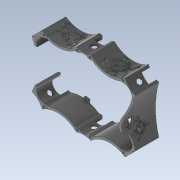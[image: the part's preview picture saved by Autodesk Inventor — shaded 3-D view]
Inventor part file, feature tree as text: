
AUTODESK INVENTOR PART (.ipt)
format: ipt  version: 2020 (Build 240168000, 168)  size: 5,370,368 bytes
history: native  units: mm
features: projected_geometry x82, extrude x36, sketch x35, other x23, reference x22, chamfer x10, plane x10, hole x3, fillet x3, emboss x3, mirror x3
ambient origin geometry x8: Origin, YZ Plane, XZ Plane, XY Plane, X Axis, Y Axis, Z Axis, Center Point
bodies: Solid1 (feature_tree), Solid2 (feature_tree)
feature tree (230):
  other  "BodyTop2.ipt"
  extrude  "Extrusion1"  Depth=4.404mm
  extrude  "Extrusion2"  Depth=22.0mm
  extrude  "Extrusion3"  Depth=35.3mm
  hole  "Hole2"  [1 undecoded]
  extrude  "Extrusion17"  Depth=19.0mm
  sketch  "Sketch27"  dims[d10=6.0mm d11=10.0mm]
  hole  "Hole4"  [1 undecoded]
  extrude  "Extrusion27"  Depth=100.0mm
  extrude  "Extrusion29"  Depth=17.453293mm
  extrude  "Extrusion30"  Depth=13.962634mm
  extrude  "Extrusion31"  Depth=4.8mm
  extrude  "Extrusion34"  Depth=6.2mm
  hole  "Hole6"  [1 undecoded]
  chamfer  "Chamfer12"  Distance=155.440339mm
  extrude  "Extrusion46"  Depth=2.0mm
  chamfer  "Chamfer13"  Distance=2.0mm
  chamfer  "Chamfer14"  Distance=4.8mm
  chamfer  "Chamfer15"  Distance=33.0mm
  chamfer  "Chamfer16"  Distance=2.5mm
  chamfer  "Chamfer17"  Distance=2.0mm
  chamfer  "Chamfer18"  Distance=2.5mm
  sketch  "Sketch55"  dims[d20=6.2mm d21=6.2mm]
  plane  "Work Plane2"
  extrude  "Extrusion55"  Depth=2.0mm
  extrude  "Extrusion56"  Depth=14.0mm
  extrude  "Extrusion57"  Depth=2.0mm
  extrude  "Extrusion61"  Depth=106.731156mm
  extrude  "Extrusion62"  Depth=94.331156mm
  extrude  "Extrusion63"  Depth=10.0mm TaperAngle=0.0deg
  extrude  "Extrusion64"  Depth=146.583126mm
  extrude  "Extrusion69"  Depth=113.583126mm
  extrude  "Extrusion70"  Depth=207.691804mm
  chamfer  "Chamfer19"  Distance=235.691804mm
  extrude  "Extrusion71"  Depth=89.108678mm
  extrude  "Extrusion72"  Depth=12.4mm
  extrude  "Extrusion73"  Depth=56.108678mm
  extrude  "Extrusion74"  Depth=12.4mm
  chamfer  "Chamfer20"  Distance=23.0mm
  extrude  "Extrusion78"  Depth=142.600153mm
  extrude  "Extrusion79"  Depth=170.600153mm
  sketch  "Sketch82"  dims[d37=6.2mm]
  extrude  "Extrusion81"  Depth=142.600153mm
  extrude  "Extrusion82"  Depth=19.0mm TaperAngle=0.0deg
  extrude  "Extrusion83"  Depth=5.0mm TaperAngle=0.0deg
  extrude  "Extrusion84"  Depth=9.0mm TaperAngle=0.0deg
  plane  "Work Plane5"
  extrude  "Extrusion86"  Depth=3.2505mm
  fillet  "Fillet2"  Radius=3.2505mm
  extrude  "Extrusion87"  Depth=3.2505mm
  fillet  "Fillet4"  Radius=3.2505mm
  plane  "Work Plane6"
  extrude  "Extrusion89"  Depth=3.2505mm
  fillet  "Fillet5"  Radius=2.4mm
  extrude  "Extrusion90"  Depth=3.1mm
  plane  "Work Plane7"
  emboss  "Emboss1"
  plane  "Work Plane8"
  extrude  "Extrusion92"  Depth=6.0mm
  plane  "Work Plane10"
  extrude  "Extrusion93"  Depth=4.5mm
  plane  "Work Plane11"
  plane  "Work Plane13"
  plane  "Work Plane14"
  plane  "Work Plane15"
  extrude  "Extrusion94"  Depth=4.5mm
  mirror  "Mirror3"
  mirror  "Mirror4"
  emboss  "Emboss3"
  emboss  "Emboss4"
  mirror  "Mirror5"
  chamfer  "Chamfer21"  Distance=1.7mm
  sketch  "Sketch1"  dims[d0=50.0mm d1=4.404mm]
  reference  "Reference1"
  reference  "Reference2"
  reference  "Reference3"
  reference  "Reference4"
  sketch  "Sketch2"  dims[d2=135.0deg d3=22.0mm]
  reference  "Reference5"
  reference  "Reference6"
  reference  "Reference7"
  reference  "Reference8"
  reference  "Reference9"
  reference  "Reference10"
  reference  "Reference11"
  reference  "Reference12"
  reference  "Reference13"
  reference  "Reference14"
  reference  "Reference15"
  reference  "Reference16"
  sketch  "Sketch3"  dims[d4=35.3mm d5=35.3mm]
  projected_geometry  "Projected Loop1"
  projected_geometry  "Projected Loop2"
  sketch  "Sketch6"  dims[d6=98.287843mm d7=10.0mm]
  reference  "Reference23"
  reference  "Reference24"
  reference  "Reference25"
  reference  "Reference26"
  reference  "Reference27"
  reference  "Reference28"
  sketch  "Sketch18"  dims[d8=19.0mm d9=19.0mm]
  projected_geometry  "Projected Loop13"
  projected_geometry  "Projected Loop19"
  projected_geometry  "Projected Loop23"
  projected_geometry  "Projected Loop28"
  projected_geometry  "Projected Loop29"
  projected_geometry  "Projected Loop30"
  sketch  "Sketch28"  dims[d12=19.0mm d13=100.0mm]
  projected_geometry  "Projected Loop31"
  projected_geometry  "Projected Loop33"
  projected_geometry  "Projected Loop34"
  sketch  "Sketch32"  dims[d14=30.0mm d15=17.453293mm]
  projected_geometry  "Projected Loop35"
  projected_geometry  "Projected Loop36"
  projected_geometry  "Projected Loop37"
  projected_geometry  "Projected Loop38"
  projected_geometry  "Projected Loop39"
  projected_geometry  "Projected Loop40"
  projected_geometry  "Projected Loop41"
  projected_geometry  "Projected Loop42"
  projected_geometry  "Projected Loop43"
  projected_geometry  "Projected Loop44"
  projected_geometry  "Projected Loop45"
  projected_geometry  "Projected Loop46"
  sketch  "Sketch35"  dims[d16=30.0mm d17=13.962634mm]
  projected_geometry  "Projected Loop52"
  sketch  "Sketch46"  dims[d18=2.0mm d19=4.8mm]
  projected_geometry  "Projected Loop74"
  sketch  "Sketch56"  dims[d22=33.0mm d23=2.5mm]
  projected_geometry  "Projected Loop75"
  sketch  "Sketch57"  dims[d24=2.0mm]
  projected_geometry  "Projected Loop76"
  sketch  "Sketch60"  dims[d25=2.5mm]
  sketch  "Sketch61"  dims[d26=2.0mm]
  projected_geometry  "Projected Loop77"
  other  "Solid1::BodyTop2.ipt"
  other  "TaggingFeature1"
  sketch  "Sketch62"  dims[d27=2.0mm]
  projected_geometry  "Projected Loop78"
  projected_geometry  "Projected Loop79"
  sketch  "Sketch69"  dims[d28=90.0deg]
  projected_geometry  "Projected Loop84"
  sketch  "Sketch70"  dims[d29=6.2mm]
  projected_geometry  "Projected Loop85"
  sketch  "Sketch71"  dims[d30=6.2mm]
  projected_geometry  "Projected Loop86"
  projected_geometry  "Projected Loop87"
  projected_geometry  "Projected Loop88"
  projected_geometry  "Projected Loop89"
  projected_geometry  "Projected Loop90"
  projected_geometry  "Projected Loop91"
  projected_geometry  "Projected Loop92"
  sketch  "Sketch72"  dims[d31=33.0mm]
  projected_geometry  "Projected Loop93"
  sketch  "Sketch73"  dims[d32=2.0mm]
  projected_geometry  "Projected Loop94"
  sketch  "Sketch74"  dims[d33=2.5mm]
  projected_geometry  "Projected Loop95"
  sketch  "Sketch78"  dims[d35=2.0mm]
  projected_geometry  "Projected Loop105"
  projected_geometry  "Projected Loop107"
  sketch  "Sketch79"  dims[d36=4.8mm]
  projected_geometry  "Projected Loop108"
  projected_geometry  "Projected Loop111"
  projected_geometry  "Projected Loop112"
  projected_geometry  "Projected Loop113"
  projected_geometry  "Projected Loop114"
  projected_geometry  "Projected Loop115"
  sketch  "Sketch83"  dims[d38=6.2mm]
  projected_geometry  "Projected Loop116"
  projected_geometry  "Projected Loop117"
  projected_geometry  "Projected Loop118"
  projected_geometry  "Projected Loop119"
  sketch  "Sketch84"  dims[d39=33.0mm]
  projected_geometry  "Projected Loop120"
  projected_geometry  "Projected Loop121"
  projected_geometry  "Projected Loop122"
  projected_geometry  "Projected Loop123"
  projected_geometry  "Projected Loop125"
  projected_geometry  "Projected Loop126"
  sketch  "Sketch89"  dims[d40=2.5mm]
  sketch  "Sketch91"  dims[d41=2.0mm]
  projected_geometry  "Projected Loop128"
  projected_geometry  "Projected Loop129"
  projected_geometry  "Projected Loop130"
  projected_geometry  "Projected Loop131"
  projected_geometry  "Projected Loop132"
  projected_geometry  "Projected Loop133"
  projected_geometry  "Projected Loop134"
  projected_geometry  "Projected Loop135"
  projected_geometry  "Projected Loop136"
  sketch  "Sketch93"  dims[d42=2.5mm]
  projected_geometry  "Projected Loop138"
  sketch  "Sketch94"  dims[d43=2.0mm]
  projected_geometry  "Projected Loop139"
  projected_geometry  "Projected Loop140"
  projected_geometry  "Projected Loop141"
  projected_geometry  "Projected Loop142"
  projected_geometry  "Projected Loop143"
  projected_geometry  "Projected Loop144"
  sketch  "Sketch96"  dims[d44=2.0mm]
  projected_geometry  "Projected Loop147"
  sketch  "Sketch97"  dims[d45=2.5mm]
  projected_geometry  "Projected Loop148"
  sketch  "Sketch98"  dims[d46=19.402mm]
  projected_geometry  "Projected Loop149"
  projected_geometry  "Projected Loop150"
  projected_geometry  "Projected Loop151"
  sketch  "Sketch99"  dims[d47=169.440339mm d48=155.440339mm d58=2.0mm d59=2.0mm d71=4.8mm d72=33.0mm d73=2.5mm d74=2.0mm d75=2.5mm d76=2.0mm d77=14.0mm d78=2.0mm d79=106.731156mm d80=94.331156mm d81=10.0mm d82=0.0mm d83=146.583126mm d84=113.583126mm d85=207.691804mm d86=235.691804mm d87=89.108678mm d88=12.4mm d89=56.108678mm d90=12.4mm d91=23.0mm d92=142.600153mm d93=170.600153mm d94=142.600153mm d95=19.0mm d96=0.0mm d97=5.0mm d98=0.0mm d153=10.0mm d154=6.0mm d155=4.0mm d156=2.0mm d157=90.0deg d158=3.8mm d159=0.0mm d310=9.0mm d311=0.0mm d382=3.0mm d383=6.0mm d384=4.0mm d385=2.0mm d386=90.0deg d387=24.0mm d388=0.0mm d396=3.2505mm d397=3.2505mm d398=3.2505mm d400=3.2505mm d401=3.2505mm d402=2.4mm d403=0.0mm d416=3.1mm d455=6.0mm d456=4.5mm d457=4.5mm d458=1.7mm d459=12.4mm d460=6.0mm d461=4.5mm d462=4.5mm d463=6.0mm d464=4.5mm d465=4.5mm d466=6.0mm d467=4.5mm d468=4.5mm d472=6.0mm d473=4.5mm d474=4.5mm d475=4.5mm d476=4.5mm d477=6.0mm d478=154.585126mm d479=147.583126mm d480=147.583126mm d481=9.0mm d482=0.0mm d483=154.585126mm d484=90.108678mm d485=10.7mm d486=147.583126mm d489=10.0mm d490=0.0mm d491=0.0mm d492=231.691804mm d493=91.808678mm d494=139.883126mm d495=171.600153mm d496=1.7mm d497=5.0mm d498=0.0mm d523=88.2mm d524=34.2mm d525=17.1mm d526=44.1mm d527=5.0mm d528=5.0mm d529=10.0mm d530=0.0mm d592=3.0mm d593=6.0mm d594=4.0mm d595=2.0mm d596=90.0deg d597=6.5mm d598=0.0mm d660=10.0mm d661=2.0mm d662=45.0deg d663=3.1mm d664=3.1mm d665=3.1mm d666=3.1mm d667=3.1mm d668=3.1mm d669=2.4mm d670=0.0mm d696=4.75mm d697=10.0mm d698=45.0deg d699=4.75mm d700=10.0mm d701=45.0deg d702=4.75mm d703=10.0mm d704=45.0deg d705=4.75mm d706=10.0mm d707=45.0deg d708=4.75mm d709=10.0mm d710=45.0deg d711=4.75mm d712=10.0mm d713=45.0deg d720=10.25mm d721=0.0mm d722=4.0mm d723=25.0mm d724=15.0mm d725=0.0mm d726=0.0mm d727=0.15mm d728=0.15mm d729=25.0mm d730=0.0mm d741=72.5mm d742=0.0mm d743=3.251mm d744=3.251mm d745=3.251mm d746=3.251mm d747=2.4mm d748=0.0mm d749=10.0mm d750=25.754mm d751=79.587449mm d752=149.613115mm d753=149.613115mm d754=25.754mm d755=56.020422mm d756=400.0mm d757=0.0mm d758=4.0mm d759=3.1mm d760=4.0mm d761=7.5mm d762=5.269851mm d763=10.539701mm d764=3.1mm d765=1.1mm d766=0.0mm d810=8.0mm d811=6.75mm d812=4.5mm d813=2.0mm d814=0.0mm d815=1.5mm d816=1.5mm d817=4.5mm d818=10.0mm d819=0.0mm d820=2.0mm d821=2.0mm d822=45.0deg d823=12.0mm d824=0.0mm d825=12.0mm d826=0.0mm d827=30.0mm d828=45.256192mm d829=10.0mm d830=0.0mm d831=30.0mm d832=54.518307mm d833=10.0mm d834=0.0mm d835=7.5mm d836=2.0mm d837=45.0deg d844=206.25mm d845=0.0mm d846=12.0mm d847=0.0mm d848=518.0mm d849=0.0mm d857=4.0mm d858=4.0mm d859=4.0mm d860=4.0mm d861=4.0mm d862=90.0deg d863=90.0deg d864=90.0deg d865=90.0deg d866=90.0deg d867=90.0deg d868=90.0deg d869=90.0deg d870=10.0mm d871=0.0mm d872=30.0mm d873=0.0mm d874=6.0mm d875=58.655611mm d876=3.0mm d877=90.0deg d878=8.0mm d879=60.0mm d880=4.0mm d881=0.0mm d882=5.6mm d883=5.6mm d884=5.6mm d885=5.6mm d886=2.4mm d887=0.0mm d892=20.0mm d893=20.0mm d894=0.0mm d895=26.0mm d896=16.0mm d898=242.0mm d899=0.0mm d903=15.25mm d904=1.8mm d905=3.0mm d906=2.0mm d907=0.0mm d908=0.0mm d909=5.0mm d910=3.6mm d911=3.0mm d912=2.5mm d913=3.6mm d914=1.6mm d915=0.0mm d919=1.0mm d920=0.0mm d921=23.0mm d922=0.0mm d923=5.29219mm d924=0.0mm d930=120.0deg d948=1.5mm d949=1.5mm d950=9.166766mm d988=1.5mm d993=135.0deg d999=90.0deg d1000=1.5mm d1005=34.139259mm d1009=82.622806mm d1186=9.0mm d1187=10.0mm d1188=100.0mm d1189=100.0mm d1190=0.0mm d1191=0.0mm d1192=9.0mm d1193=10.0mm d1194=10.0mm d1195=0.0mm d1197=10.0mm d1198=1.5mm d1199=15.0mm d1200=15.0mm d1201=90.0deg d1202=150.0deg d1203=1.5mm d1204=1.5mm d1205=5.0mm d1206=135.0deg d1207=8.0mm d1208=45.0deg d1209=1.5mm d1210=1.5mm d1211=2.0mm d1212=2.0mm d1213=135.0deg d1214=1.5mm d1215=1.5mm d1218=7.0mm d1219=1.5mm d1220=0.0mm d1222=13.0mm d1223=135.0deg d1224=4.0mm d1225=2.0mm d1226=1.5mm d1227=1.5mm d1228=135.0deg d1229=2.0mm d1230=1.5mm d1231=1.5mm d1233=6.0mm d1234=1.5mm d1235=60.0deg d1236=135.0deg d1237=11.0mm d1238=6.0mm d1239=135.0deg d1240=3.0mm d1264=1.0mm d1265=0.0mm d1289=3.0mm d1290=135.0deg d1291=3.0mm d1302=45.0deg d1303=45.0deg d1304=2.0mm d1305=2.0mm d1306=1.5mm d1307=1.5mm d1310=10.0mm d1311=15.0mm d1312=3.0mm d1313=135.0deg d1314=15.0mm d1315=3.0mm d1316=135.0deg d1317=3.0mm d1318=135.0deg d1319=3.0mm d1320=135.0deg d1321=1.5mm d1322=1.5mm d1323=1.5mm d1324=1.5mm d1325=1.5mm d1326=1.5mm d1327=1.5mm d1328=1.5mm d1329=0.75mm d1330=4.0mm d1331=1.5mm d1332=1.5mm d1333=1.5mm d1334=1.5mm d1335=0.75mm d1336=4.0mm d1337=1.5mm d1338=4.0mm d1339=1.5mm d1340=4.0mm d1341=1.5mm d1342=4.0mm d1343=1.5mm d1344=4.0mm d1345=2.0mm d1348=5.0mm d1349=2.0mm d1350=45.0deg d1351=1.5mm d1352=1.5mm d1353=2.0mm d1354=45.0deg d1355=1.5mm d1356=4.0mm d1357=135.0deg d1358=5.0mm d1359=6.0mm d1360=135.0deg d1361=135.0deg d1362=2.0mm d1363=45.0deg d1364=1.5mm d1365=2.0mm d1366=45.0deg d1367=1.5mm d1368=135.0deg d1369=90.0deg d1370=7.0mm d1371=43.03052mm d1372=1.5mm d1373=10.0mm d1374=1.5mm d1375=15.0mm d1376=15.0mm d1377=90.0deg d1378=150.0deg d1379=1.5mm d1380=1.5mm d1381=5.0mm d1382=135.0deg d1383=8.0mm d1384=45.0deg d1385=1.5mm d1386=1.5mm d1387=2.0mm d1388=2.0mm d1389=135.0deg d1390=1.5mm d1391=1.5mm d1392=7.0mm d1393=1.5mm d1394=0.0mm d1395=13.0mm d1396=135.0deg d1397=4.0mm d1398=2.0mm d1399=1.5mm d1400=1.5mm d1401=135.0deg d1402=2.0mm d1403=1.5mm d1404=1.5mm d1405=6.0mm d1406=1.5mm d1407=60.0deg d1408=135.0deg d1409=11.0mm d1410=6.0mm d1411=135.0deg d1412=3.0mm d1413=3.0mm d1414=135.0deg d1415=3.0mm d1416=45.0deg d1417=45.0deg d1418=2.0mm d1419=2.0mm d1420=1.5mm d1421=1.5mm d1422=10.0mm d1423=15.0mm d1424=3.0mm d1425=135.0deg d1426=15.0mm d1427=3.0mm d1428=135.0deg d1429=3.0mm d1430=135.0deg d1431=3.0mm d1432=135.0deg d1433=1.5mm d1434=1.5mm d1435=1.5mm d1436=1.5mm d1437=1.5mm d1438=1.5mm d1439=1.5mm d1440=1.5mm d1441=0.75mm d1442=4.0mm d1443=1.5mm d1444=1.5mm d1445=1.5mm d1446=1.5mm d1447=0.75mm d1448=4.0mm d1449=1.5mm d1450=4.0mm d1451=1.5mm d1452=4.0mm d1453=1.5mm d1454=4.0mm d1455=1.5mm d1456=4.0mm d1457=2.0mm d1458=5.0mm d1459=2.0mm d1460=45.0deg d1461=1.5mm d1462=1.5mm d1463=2.0mm d1464=45.0deg d1465=1.5mm d1466=4.0mm d1467=135.0deg d1468=5.0mm d1469=6.0mm d1470=135.0deg d1471=135.0deg d1472=2.0mm d1473=45.0deg d1474=1.5mm d1475=2.0mm d1476=45.0deg d1477=1.5mm d1478=135.0deg d1479=90.0deg d1480=7.0mm d1481=43.03052mm d1482=1.5mm d1483=1.0mm d1484=0.0mm d1485=0.75mm d1486=3.0mm d1487=0.75mm d1488=0.75mm d1489=0.75mm d1490=6.0mm d1491=0.75mm d1492=1.5mm d1493=4.0mm d1494=1.5mm d1495=4.0mm d1496=4.0mm d1498=6.0mm d1499=4.0mm d1500=135.0deg d1501=2.0mm d1502=45.0deg d1503=1.5mm d1504=90.0deg d1505=1.5mm d1506=135.0deg d1507=3.5mm d1508=1.5mm d1509=1.5mm d1510=1.5mm d1511=1.5mm d1512=4.0mm d1513=1.56mm d1514=4.0mm d1515=1.5mm d1516=4.0mm d1517=1.5mm d1518=2.0mm d1519=135.0deg d1520=1.5mm d1521=2.0mm d1522=45.0deg d1523=1.5mm d1524=1.5mm d1525=2.0mm d1526=135.0deg d1527=3.0mm d1528=1.5mm d1529=1.5mm d1530=1.5mm d1531=4.0mm d1532=1.5mm d1533=4.0mm d1534=1.5mm d1536=1.5mm d1538=0.75mm d1539=0.75mm d1540=4.0mm d1542=1.5mm d1543=4.0mm d1544=1.5mm d1545=4.0mm d1546=1.5mm d1547=4.0mm d1548=1.5mm d1550=1.5mm d1551=1.5mm d1555=2.0mm d1556=2.0mm d1557=60.0deg d1558=1.0mm d1560=6.0mm d1561=2.0mm d1562=2.0mm d1563=60.0deg d1564=6.0mm d1565=1.0mm d1566=6.0mm d1567=2.0mm d1568=60.0deg d1569=1.0mm d1571=8.484773mm d1572=10.395572mm d1573=5.930716mm d1574=27.445097mm d1575=1.0mm d1576=2.0mm d1577=45.0deg d99=0.5mm d100=0.872665mm d160=0.5mm d161=0.872665mm d162=0.5mm d163=0.872665mm d171=0.5mm d172=0.872665mm d173=0.5mm d174=0.872665mm d191=0.5mm d192=0.872665mm d193=0.5mm d194=0.872665mm d205=0.5mm d206=0.872665mm d207=0.5mm d208=0.872665mm d244=0.5mm d245=0.872665mm d246=0.5mm d247=0.872665mm d307=0.5mm d308=0.872665mm d309=0.5mm d352=0.5mm d353=0.872665mm d354=0.5mm d355=0.872665mm d412=0.5mm d413=0.872665mm d414=0.5mm d415=0.872665mm d417=0.872665mm d586=0.5mm d587=0.872665mm d588=0.5mm d589=0.872665mm d838=0.5mm d839=0.872665mm d840=0.5mm d841=0.872665mm d842=0.5mm d843=0.872665mm d855=0.5mm d856=0.872665mm]
  projected_geometry  "Projected Loop152"
  other  "<userpath>\Documents\Inventor Projects\SpiderTest\Test3\SpiderLegDemo.iam"
  other  "SpiderLegDemo.iam"
  other  "Tower Pro MG90S Micro servo:1"
  other  "Крышка корпуса задняя:1"
  other  "Крышка корпуса:1"
  other  "LegSup:1"
  other  "<userpath>\Documents\Inventor Projects\SpiderTest\Test5\Demo.iam"
  other  "Demo.iam"
  other  "SpiderLegDemoRight:1"
  other  "SpiderLegDemoRight:5"
  other  "<userpath>\Documents\Inventor Projects\SpiderTest\Test3\Demo.iam"
  other  "SpiderLegDemo:3"
  other  "SpiderLegDemo:4"
  other  "SpiderLegDemo:2"
  other  "SpiderLegDemoRight:6"
  other  "SpiderLegDemoLeft:2"
  other  "Вал последний с чем то:1"
  other  "SpiderLegDemoLeft:3"
  other  "ограничитель:2"
  other  "SpiderLegDemoLeft:1"
note: 3 required parameter values undecoded (feature->parameter linkage not recoverable at this tier; creation-order binding heuristic only, values carry confidence <= 0.55)
